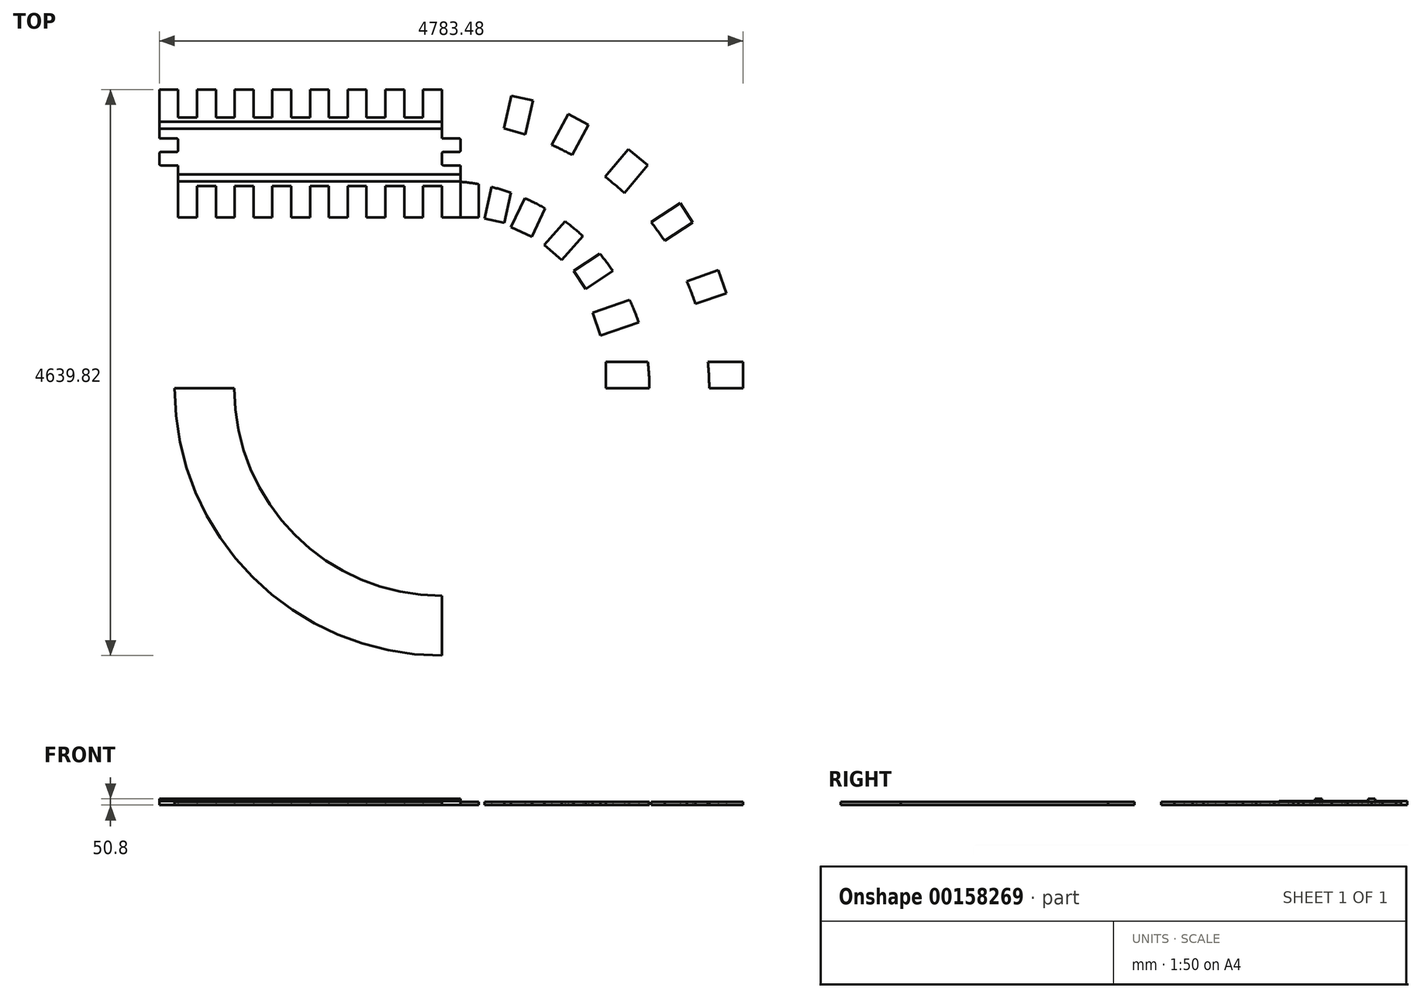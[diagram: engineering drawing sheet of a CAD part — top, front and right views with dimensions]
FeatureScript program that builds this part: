
annotation { "Feature Type Name" : "Feature", "Feature Type Description" : "" }
export const myFeature = defineFeature(function(context is Context, id is Id, definition is map)
    precondition{}
    {
        {
            var Q0;
            Q0=qCreatedBy(makeId("Top.planeOp"),FACE);
            var sketch = newSketch(context, id + "F0", { "sketchPlane" : qUnion([Q0])});
            skLineSegment(sketch, "E0", {"start": v(0, 0) * mm, "end": v(141.6, 0) * mm});
            skLineSegment(sketch, "E1", {"start": v(154.3, -12.7) * mm, "end": v(154.3, -97.3) * mm});
            skLineSegment(sketch, "E2", {"start": v(141.6, -110) * mm, "end": v(12.7, -110) * mm});
            skLineSegment(sketch, "E3", {"start": v(0, -122.7) * mm, "end": v(0, -207.32) * mm});
            skLineSegment(sketch, "E4", {"start": v(12.7, -220.02) * mm, "end": v(154.3, -220.02) * mm});
            skLineSegment(sketch, "E5", {"start": v(154.3, -220.02) * mm, "end": v(154.3, -647.87) * mm});
            skLineSegment(sketch, "E6", {"start": v(154.3, -647.87) * mm, "end": v(0, -647.87) * mm});
            skLineSegment(sketch, "E7", {"start": v(0, -647.87) * mm, "end": v(0, -389.82) * mm});
            skLineSegment(sketch, "E8", {"start": v(0, -389.82) * mm, "end": v(-154.3, -389.82) * mm});
            skLineSegment(sketch, "E9", {"start": v(-154.3, -389.82) * mm, "end": v(-154.3, -647.87) * mm});
            skLineSegment(sketch, "E10", {"start": v(-154.3, -647.87) * mm, "end": v(-308.61, -647.87) * mm});
            skLineSegment(sketch, "E11", {"start": v(-308.61, -647.87) * mm, "end": v(-308.61, -389.82) * mm});
            skLineSegment(sketch, "E12", {"start": v(-308.61, -389.82) * mm, "end": v(-462.92, -389.82) * mm});
            skLineSegment(sketch, "E13", {"start": v(-462.92, -389.82) * mm, "end": v(-462.92, -647.87) * mm});
            skLineSegment(sketch, "E14", {"start": v(-462.92, -647.87) * mm, "end": v(-617.22, -647.87) * mm});
            skLineSegment(sketch, "E15", {"start": v(-617.22, -647.87) * mm, "end": v(-617.22, -389.82) * mm});
            skLineSegment(sketch, "E16", {"start": v(-617.22, -389.82) * mm, "end": v(-771.53, -389.82) * mm});
            skLineSegment(sketch, "E17", {"start": v(-771.53, -389.82) * mm, "end": v(-771.53, -647.87) * mm});
            skLineSegment(sketch, "E18", {"start": v(-771.53, -647.87) * mm, "end": v(-925.83, -647.87) * mm});
            skLineSegment(sketch, "E19", {"start": v(-925.83, -647.87) * mm, "end": v(-925.83, -389.82) * mm});
            skPoint(sketch, "E20.visualSharp", {"position": v(154.3, 0) * mm});
            skArc(sketch, "E20.filletArc", {"start": v(154.3, -12.7) * mm, "mid": v(150.59, -3.72) * mm, "end": v(141.6, 0) * mm});
            skPoint(sketch, "E21.visualSharp", {"position": v(154.3, -110) * mm});
            skArc(sketch, "E21.filletArc", {"start": v(141.6, -110) * mm, "mid": v(150.59, -106.29) * mm, "end": v(154.3, -97.3) * mm});
            skPoint(sketch, "E22.visualSharp", {"position": v(0, -220.02) * mm});
            skArc(sketch, "E22.filletArc", {"start": v(0, -207.32) * mm, "mid": v(3.72, -216.3) * mm, "end": v(12.7, -220.02) * mm});
            skPoint(sketch, "E23.visualSharp", {"position": v(0, -110) * mm});
            skArc(sketch, "E23.filletArc", {"start": v(12.7, -110) * mm, "mid": v(3.72, -113.73) * mm, "end": v(0, -122.7) * mm});
            skLineSegment(sketch, "E24", {"start": v(-925.83, -389.82) * mm, "end": v(-1080.14, -389.82) * mm});
            skLineSegment(sketch, "E25", {"start": v(-1080.14, -389.82) * mm, "end": v(-1080.14, -647.87) * mm});
            skLineSegment(sketch, "E26", {"start": v(-1080.14, -647.87) * mm, "end": v(-1234.44, -647.87) * mm});
            skLineSegment(sketch, "E27", {"start": v(-1234.44, -647.87) * mm, "end": v(-1234.44, -389.82) * mm});
            skLineSegment(sketch, "E28", {"start": v(-1234.44, -389.82) * mm, "end": v(-1388.75, -389.82) * mm});
            skLineSegment(sketch, "E29", {"start": v(-1388.75, -389.82) * mm, "end": v(-1388.75, -647.87) * mm});
            skLineSegment(sketch, "E30", {"start": v(-1388.75, -647.87) * mm, "end": v(-1543.05, -647.87) * mm});
            skLineSegment(sketch, "E31", {"start": v(-1543.05, -647.87) * mm, "end": v(-1543.05, -389.82) * mm});
            skLineSegment(sketch, "E32", {"start": v(-1543.05, -389.82) * mm, "end": v(-1697.36, -389.82) * mm});
            skLineSegment(sketch, "E33", {"start": v(-1697.36, -389.82) * mm, "end": v(-1697.36, -647.87) * mm});
            skLineSegment(sketch, "E34", {"start": v(-1697.36, -647.87) * mm, "end": v(-1851.67, -647.87) * mm});
            skLineSegment(sketch, "E35", {"start": v(-1851.67, -647.87) * mm, "end": v(-1851.67, -389.82) * mm});
            skLineSegment(sketch, "E36", {"start": v(-1851.67, -389.82) * mm, "end": v(-2005.97, -389.82) * mm});
            skLineSegment(sketch, "E37", {"start": v(-2005.97, -389.82) * mm, "end": v(-2005.97, -647.87) * mm});
            skLineSegment(sketch, "E38", {"start": v(-2005.97, -647.87) * mm, "end": v(-2160.29, -647.87) * mm});
            skLineSegment(sketch, "E39", {"start": v(-2160.29, -647.87) * mm, "end": v(-2160.29, -220.02) * mm});
            skLineSegment(sketch, "E40", {"start": v(-2160.29, -220.02) * mm, "end": v(-2301.9, -220.02) * mm});
            skLineSegment(sketch, "E41", {"start": v(-2314.6, -207.32) * mm, "end": v(-2314.6, -122.7) * mm});
            skLineSegment(sketch, "E42", {"start": v(-2301.9, -110) * mm, "end": v(-2172.99, -110) * mm});
            skLineSegment(sketch, "E43", {"start": v(-2160.29, -97.3) * mm, "end": v(-2160.29, -12.7) * mm});
            skLineSegment(sketch, "E44", {"start": v(-2172.99, 0) * mm, "end": v(-2314.6, 0) * mm});
            skLineSegment(sketch, "E45", {"start": v(-2314.6, 0) * mm, "end": v(-2314.6, 399.88) * mm});
            skPoint(sketch, "E46.visualSharp", {"position": v(-2314.6, -110) * mm});
            skArc(sketch, "E46.filletArc", {"start": v(-2301.9, -110) * mm, "mid": v(-2310.87, -113.73) * mm, "end": v(-2314.6, -122.7) * mm});
            skPoint(sketch, "E47.visualSharp", {"position": v(-2314.6, -220.02) * mm});
            skArc(sketch, "E47.filletArc", {"start": v(-2314.6, -207.32) * mm, "mid": v(-2310.87, -216.3) * mm, "end": v(-2301.9, -220.02) * mm});
            skPoint(sketch, "E48.visualSharp", {"position": v(-2160.29, -110) * mm});
            skArc(sketch, "E48.filletArc", {"start": v(-2172.99, -110) * mm, "mid": v(-2164, -106.29) * mm, "end": v(-2160.29, -97.3) * mm});
            skPoint(sketch, "E49.visualSharp", {"position": v(-2160.29, 0) * mm});
            skArc(sketch, "E49.filletArc", {"start": v(-2160.29, -12.7) * mm, "mid": v(-2164, -3.72) * mm, "end": v(-2172.99, 0) * mm});
            skLineSegment(sketch, "E50", {"start": v(-2314.6, 399.88) * mm, "end": v(-2160.29, 399.88) * mm});
            skLineSegment(sketch, "E51", {"start": v(-2160.29, 399.88) * mm, "end": v(-2160.29, 172.14) * mm});
            skLineSegment(sketch, "E52", {"start": v(-2160.29, 172.14) * mm, "end": v(-2005.98, 172.14) * mm});
            skLineSegment(sketch, "E53", {"start": v(-2005.98, 172.14) * mm, "end": v(-2005.98, 399.88) * mm});
            skLineSegment(sketch, "E54", {"start": v(-2005.98, 399.88) * mm, "end": v(-1851.68, 399.88) * mm});
            skLineSegment(sketch, "E55", {"start": v(-1851.68, 399.88) * mm, "end": v(-1851.68, 172.14) * mm});
            skLineSegment(sketch, "E56", {"start": v(-1851.68, 172.14) * mm, "end": v(-1697.37, 172.14) * mm});
            skLineSegment(sketch, "E57", {"start": v(-1697.37, 172.14) * mm, "end": v(-1697.37, 399.88) * mm});
            skLineSegment(sketch, "E58", {"start": v(-1697.37, 399.88) * mm, "end": v(-1543.07, 399.88) * mm});
            skLineSegment(sketch, "E59", {"start": v(-1543.07, 399.88) * mm, "end": v(-1543.07, 172.14) * mm});
            skLineSegment(sketch, "E60", {"start": v(-1543.07, 172.14) * mm, "end": v(-1388.76, 172.14) * mm});
            skLineSegment(sketch, "E61", {"start": v(-1388.76, 172.14) * mm, "end": v(-1388.76, 400.96) * mm});
            skLineSegment(sketch, "E62", {"start": v(-1388.76, 400.96) * mm, "end": v(-1234.46, 400.96) * mm});
            skLineSegment(sketch, "E63", {"start": v(-1234.46, 400.96) * mm, "end": v(-1234.46, 172.14) * mm});
            skLineSegment(sketch, "E64", {"start": v(-1234.46, 172.14) * mm, "end": v(-1080.15, 172.14) * mm});
            skLineSegment(sketch, "E65", {"start": v(-1080.15, 172.14) * mm, "end": v(-1080.15, 400.96) * mm});
            skLineSegment(sketch, "E66", {"start": v(-1080.15, 400.96) * mm, "end": v(-925.85, 400.96) * mm});
            skLineSegment(sketch, "E67", {"start": v(-925.85, 400.96) * mm, "end": v(-925.85, 172.14) * mm});
            skLineSegment(sketch, "E68", {"start": v(-925.85, 172.14) * mm, "end": v(-771.54, 172.14) * mm});
            skLineSegment(sketch, "E69", {"start": v(-771.54, 172.14) * mm, "end": v(-771.54, 400.96) * mm});
            skLineSegment(sketch, "E70", {"start": v(-771.54, 400.96) * mm, "end": v(-617.24, 400.96) * mm});
            skLineSegment(sketch, "E71", {"start": v(-617.24, 400.96) * mm, "end": v(-617.24, 172.14) * mm});
            skLineSegment(sketch, "E72", {"start": v(-617.24, 172.14) * mm, "end": v(-462.93, 172.14) * mm});
            skLineSegment(sketch, "E73", {"start": v(-462.93, 172.14) * mm, "end": v(-462.93, 400.96) * mm});
            skLineSegment(sketch, "E74", {"start": v(-462.93, 400.96) * mm, "end": v(-308.63, 400.96) * mm});
            skLineSegment(sketch, "E75", {"start": v(-308.63, 400.96) * mm, "end": v(-308.63, 172.14) * mm});
            skLineSegment(sketch, "E76", {"start": v(-308.63, 172.14) * mm, "end": v(-154.32, 172.14) * mm});
            skLineSegment(sketch, "E77", {"start": v(-154.32, 172.14) * mm, "end": v(-154.32, 400.96) * mm});
            skLineSegment(sketch, "E78", {"start": v(-154.32, 400.96) * mm, "end": v(-0.02, 400.96) * mm});
            skLineSegment(sketch, "E79", {"start": v(-0.02, 400.96) * mm, "end": v(-0.02, 172.14) * mm});
            skLineSegment(sketch, "E80", {"start": v(-0.02, 172.14) * mm, "end": v(0, 0) * mm});
            skSolve(sketch);
        }
        {
            var Q0;
            Q0=makeQuery(id+"F0.imprint","IMPRINT",FACE,{"disambiguationData":[TD([[makeQuery(id+"F0.imprint","IMPRINT",EDGE,{"derivedFrom":sQuery(id+"F0.wireOp",EDGE,"E0")}),-1.0]])]});
            var sketch = newSketch(context, id + "F1", { "sketchPlane" : qUnion([Q0])});
            skLineSegment(sketch, "E81", {"start": v(-2314.86, 138.26) * mm, "end": v(0, 138.26) * mm});
            skLineSegment(sketch, "E82.0", {"start": v(-2314.86, 81.11) * mm, "end": v(0, 81.11) * mm});
            skLineSegment(sketch, "E83", {"start": v(-2160.59, -353.29) * mm, "end": v(154.12, -353.29) * mm});
            skLineSegment(sketch, "E84.0", {"start": v(-2160.59, -296.14) * mm, "end": v(154.12, -296.14) * mm});
            skLineSegment(sketch, "E85", {"start": v(-2314.86, 138.26) * mm, "end": v(-2314.86, 81.11) * mm});
            skLineSegment(sketch, "E86", {"start": v(-2160.59, -296.14) * mm, "end": v(-2160.59, -353.29) * mm});
            skLineSegment(sketch, "E87", {"start": v(154.12, -296.14) * mm, "end": v(154.12, -353.29) * mm});
            skLineSegment(sketch, "E88", {"start": v(0, 138.26) * mm, "end": v(0, 81.11) * mm});
            skSolve(sketch);
        }
        {
            var Q0;
            Q0=qSketchRegion(id+"F0",true);
            extrude(context, id + "F2", {"entities" : qUnion([Q0]), "depth" : 31.75 * mm});
        }
        {
            var Q0;
            Q0=qSketchRegion(id+"F1",true);
            extrude(context, id + "F3", {"entities" : qUnion([Q0]), "operationType" : NewBodyOperationType.ADD, "depth" : 50.8 * mm});
        }
        {
            var Q0;
            Q0=qCreatedBy(makeId("Top.planeOp"),FACE);
            var sketch = newSketch(context, id + "F4", { "sketchPlane" : qUnion([Q0])});
            skCircle(sketch, "E89", {"center": v(0, -2048.58) * mm, "radius": 2190.28 * mm});
            skCircle(sketch, "E90", {"center": v(0, -2048.58) * mm, "radius": 1700.76 * mm});
            skLineSegment(sketch, "E91", {"start": v(0, -4987.67) * mm, "end": v(0, 1254.96) * mm});
            skLineSegment(sketch, "E92", {"start": v(-3366.62, -2048.58) * mm, "end": v(3747.67, -2048.58) * mm});
            skLineSegment(sketch, "E93", {"start": v(0, 141.7) * mm, "end": v(0, 0) * mm});
            skLineSegment(sketch, "E94", {"start": v(0, 0) * mm, "end": v(142.26, 0) * mm});
            skLineSegment(sketch, "E95", {"start": v(154.96, -12.7) * mm, "end": v(154.96, -96.46) * mm});
            skLineSegment(sketch, "E96", {"start": v(142.26, -109.16) * mm, "end": v(12.7, -109.16) * mm});
            skLineSegment(sketch, "E97", {"start": v(0, -121.86) * mm, "end": v(0, -207.92) * mm});
            skLineSegment(sketch, "E98", {"start": v(12.7, -220.62) * mm, "end": v(153.58, -220.62) * mm});
            skLineSegment(sketch, "E99", {"start": v(153.58, -220.62) * mm, "end": v(153.58, -354.76) * mm});
            skPoint(sketch, "E100.visualSharp", {"position": v(154.96, 0) * mm});
            skArc(sketch, "E100.filletArc", {"start": v(154.96, -12.7) * mm, "mid": v(151.24, -3.72) * mm, "end": v(142.26, 0) * mm});
            skPoint(sketch, "E101.visualSharp", {"position": v(154.96, -109.16) * mm});
            skArc(sketch, "E101.filletArc", {"start": v(142.26, -109.16) * mm, "mid": v(151.24, -105.44) * mm, "end": v(154.96, -96.46) * mm});
            skPoint(sketch, "E102.visualSharp", {"position": v(0, -220.62) * mm});
            skArc(sketch, "E102.filletArc", {"start": v(0, -207.92) * mm, "mid": v(3.72, -216.9) * mm, "end": v(12.7, -220.62) * mm});
            skPoint(sketch, "E103.visualSharp", {"position": v(0, -109.16) * mm});
            skArc(sketch, "E103.filletArc", {"start": v(12.7, -109.16) * mm, "mid": v(3.72, -112.88) * mm, "end": v(0, -121.86) * mm});
            skLineSegment(sketch, "E104", {"start": v(0, 141.7) * mm, "end": v(0, 400.95) * mm});
            skLineSegment(sketch, "E105", {"start": v(0, 400.95) * mm, "end": v(152.02, 400.95) * mm});
            skLineSegment(sketch, "E106", {"start": v(152.02, 400.95) * mm, "end": v(152.02, 136.42) * mm});
            skLineSegment(sketch, "E107", {"start": v(900.1, -51.79) * mm, "end": v(1034.84, 199.45) * mm});
            skLineSegment(sketch, "E108", {"start": v(1034.84, 199.45) * mm, "end": v(1199.5, 111.15) * mm});
            skLineSegment(sketch, "E109", {"start": v(1199.5, 111.15) * mm, "end": v(1067.06, -135.8) * mm});
            skLineSegment(sketch, "E110", {"start": v(1714.15, -685.11) * mm, "end": v(1954.38, -530.86) * mm});
            skLineSegment(sketch, "E111", {"start": v(1954.38, -530.86) * mm, "end": v(2056.05, -689.2) * mm});
            skLineSegment(sketch, "E112", {"start": v(2056.05, -689.2) * mm, "end": v(1825.03, -837.55) * mm});
            skLineSegment(sketch, "E113", {"start": v(508.33, 81.9) * mm, "end": v(568.73, 351) * mm});
            skLineSegment(sketch, "E114", {"start": v(568.73, 351) * mm, "end": v(747.33, 310.92) * mm});
            skLineSegment(sketch, "E115", {"start": v(747.33, 310.92) * mm, "end": v(684.71, 31.93) * mm});
            skLineSegment(sketch, "E116", {"start": v(1338.6, -314.95) * mm, "end": v(1527.03, -87.62) * mm});
            skLineSegment(sketch, "E117", {"start": v(1527.03, -87.62) * mm, "end": v(1684.9, -218.47) * mm});
            skLineSegment(sketch, "E118", {"start": v(1684.9, -218.47) * mm, "end": v(1494.87, -447.74) * mm});
            skLineSegment(sketch, "E119", {"start": v(2006.14, -1169.52) * mm, "end": v(2265.44, -1079.33) * mm});
            skLineSegment(sketch, "E120", {"start": v(2265.44, -1079.33) * mm, "end": v(2331.04, -1267.93) * mm});
            skLineSegment(sketch, "E121", {"start": v(2331.04, -1267.93) * mm, "end": v(2077.9, -1355.98) * mm});
            skLineSegment(sketch, "E122", {"start": v(2179.55, -1832.02) * mm, "end": v(2468.62, -1832.02) * mm});
            skLineSegment(sketch, "E123", {"start": v(2468.62, -1832.02) * mm, "end": v(2468.62, -2048.58) * mm});
            skLineSegment(sketch, "E124", {"start": v(153.58, -354.76) * mm, "end": v(153.58, -647.34) * mm});
            skLineSegment(sketch, "E125", {"start": v(153.58, -647.34) * mm, "end": v(303.64, -647.34) * mm});
            skLineSegment(sketch, "E126", {"start": v(303.64, -647.34) * mm, "end": v(303.64, -375.14) * mm});
            skLineSegment(sketch, "E127", {"start": v(406.51, -397.11) * mm, "end": v(350.84, -655.51) * mm});
            skLineSegment(sketch, "E128", {"start": v(350.84, -655.51) * mm, "end": v(511.42, -690.1) * mm});
            skLineSegment(sketch, "E129", {"start": v(511.42, -690.1) * mm, "end": v(564.4, -444.2) * mm});
            skLineSegment(sketch, "E130", {"start": v(678.89, -489.18) * mm, "end": v(566.54, -725.25) * mm});
            skLineSegment(sketch, "E131", {"start": v(566.54, -725.25) * mm, "end": v(735.75, -805.78) * mm});
            skLineSegment(sketch, "E132", {"start": v(735.75, -805.78) * mm, "end": v(846.35, -573.36) * mm});
            skLineSegment(sketch, "E133", {"start": v(1009.64, -679.92) * mm, "end": v(840.33, -871.76) * mm});
            skLineSegment(sketch, "E134", {"start": v(840.33, -871.76) * mm, "end": v(981.8, -996.63) * mm});
            skLineSegment(sketch, "E135", {"start": v(981.8, -996.63) * mm, "end": v(1155.12, -800.27) * mm});
            skLineSegment(sketch, "E136", {"start": v(1293.87, -944.72) * mm, "end": v(1081.5, -1084.9) * mm});
            skLineSegment(sketch, "E137", {"start": v(1081.5, -1084.9) * mm, "end": v(1179.42, -1233.25) * mm});
            skLineSegment(sketch, "E138", {"start": v(1179.42, -1233.25) * mm, "end": v(1402.27, -1086.17) * mm});
            skLineSegment(sketch, "E139", {"start": v(1538.53, -1323.66) * mm, "end": v(1235.92, -1427.35) * mm});
            skLineSegment(sketch, "E140", {"start": v(1235.92, -1427.35) * mm, "end": v(1299.82, -1613.82) * mm});
            skLineSegment(sketch, "E141", {"start": v(1299.82, -1613.82) * mm, "end": v(1612.16, -1506.8) * mm});
            skLineSegment(sketch, "E142", {"start": v(1686.92, -1832.02) * mm, "end": v(1342.87, -1832.02) * mm});
            skLineSegment(sketch, "E143", {"start": v(1342.87, -1832.02) * mm, "end": v(1342.87, -2048.58) * mm});
            skSolve(sketch);
        }
        {
            var Q0;
            {var subQ0=sQuery(id+"F4.wireOp",EDGE,"E91");var subQ1=sQuery(id+"F4.wireOp",EDGE,"E89");var subQ2=makeQuery(id+"F4.imprint","INTERSECT",VERTEX,{"disambiguationData":[OD(0.0)],"derivedFrom":[subQ1,subQ0]});Q0=makeQuery(id+"F4.imprint","IMPRINT",FACE,{"disambiguationData":[TD([[makeQuery(id+"F4.imprint","IMPRINT",EDGE,{"disambiguationData":[TD([[subQ2,1.0]])],"derivedFrom":subQ1}),1.0]])]});}
            var Q1;
            {var subQ1=sQuery(id+"F4.wireOp",EDGE,"E93");Q1=makeQuery(id+"F4.imprint","IMPRINT",FACE,{"disambiguationData":[TD([[makeQuery(id+"F4.imprint","IMPRINT",EDGE,{"derivedFrom":subQ1}),1.0]])]});}
            var Q2;
            {var subQ0=sQuery(id+"F4.wireOp",EDGE,"E113");Q2=makeQuery(id+"F4.imprint","IMPRINT",FACE,{"disambiguationData":[TD([[makeQuery(id+"F4.imprint","IMPRINT",EDGE,{"derivedFrom":subQ0}),-1.0]])]});}
            var Q3;
            {var subQ0=sQuery(id+"F4.wireOp",EDGE,"E104");Q3=makeQuery(id+"F4.imprint","IMPRINT",FACE,{"disambiguationData":[TD([[makeQuery(id+"F4.imprint","IMPRINT",EDGE,{"derivedFrom":subQ0}),-1.0]])]});}
            var Q4;
            {var subQ0=sQuery(id+"F4.wireOp",EDGE,"E107");Q4=makeQuery(id+"F4.imprint","IMPRINT",FACE,{"disambiguationData":[TD([[makeQuery(id+"F4.imprint","IMPRINT",EDGE,{"derivedFrom":subQ0}),-1.0]])]});}
            var Q5;
            {var subQ0=sQuery(id+"F4.wireOp",EDGE,"E124");Q5=makeQuery(id+"F4.imprint","IMPRINT",FACE,{"disambiguationData":[TD([[makeQuery(id+"F4.imprint","IMPRINT",EDGE,{"derivedFrom":subQ0}),1.0]])]});}
            var Q6;
            {var subQ0=sQuery(id+"F4.wireOp",EDGE,"E127");Q6=makeQuery(id+"F4.imprint","IMPRINT",FACE,{"disambiguationData":[TD([[makeQuery(id+"F4.imprint","IMPRINT",EDGE,{"derivedFrom":subQ0}),1.0]])]});}
            var Q7;
            {var subQ0=sQuery(id+"F4.wireOp",EDGE,"E130");Q7=makeQuery(id+"F4.imprint","IMPRINT",FACE,{"disambiguationData":[TD([[makeQuery(id+"F4.imprint","IMPRINT",EDGE,{"derivedFrom":subQ0}),1.0]])]});}
            var Q8;
            {var subQ0=sQuery(id+"F4.wireOp",EDGE,"E133");Q8=makeQuery(id+"F4.imprint","IMPRINT",FACE,{"disambiguationData":[TD([[makeQuery(id+"F4.imprint","IMPRINT",EDGE,{"derivedFrom":subQ0}),1.0]])]});}
            var Q9;
            {var subQ0=sQuery(id+"F4.wireOp",EDGE,"E136");Q9=makeQuery(id+"F4.imprint","IMPRINT",FACE,{"disambiguationData":[TD([[makeQuery(id+"F4.imprint","IMPRINT",EDGE,{"derivedFrom":subQ0}),1.0]])]});}
            var Q10;
            {var subQ0=sQuery(id+"F4.wireOp",EDGE,"E139");Q10=makeQuery(id+"F4.imprint","IMPRINT",FACE,{"disambiguationData":[TD([[makeQuery(id+"F4.imprint","IMPRINT",EDGE,{"derivedFrom":subQ0}),1.0]])]});}
            var Q11;
            {var subQ0=sQuery(id+"F4.wireOp",EDGE,"E142");Q11=makeQuery(id+"F4.imprint","IMPRINT",FACE,{"disambiguationData":[TD([[makeQuery(id+"F4.imprint","IMPRINT",EDGE,{"derivedFrom":subQ0}),1.0]])]});}
            var Q12;
            {var subQ0=sQuery(id+"F4.wireOp",EDGE,"E122");Q12=makeQuery(id+"F4.imprint","IMPRINT",FACE,{"disambiguationData":[TD([[makeQuery(id+"F4.imprint","IMPRINT",EDGE,{"derivedFrom":subQ0}),-1.0]])]});}
            var Q13;
            {var subQ0=sQuery(id+"F4.wireOp",EDGE,"E119");Q13=makeQuery(id+"F4.imprint","IMPRINT",FACE,{"disambiguationData":[TD([[makeQuery(id+"F4.imprint","IMPRINT",EDGE,{"derivedFrom":subQ0}),-1.0]])]});}
            var Q14;
            {var subQ0=sQuery(id+"F4.wireOp",EDGE,"E110");Q14=makeQuery(id+"F4.imprint","IMPRINT",FACE,{"disambiguationData":[TD([[makeQuery(id+"F4.imprint","IMPRINT",EDGE,{"derivedFrom":subQ0}),-1.0]])]});}
            var Q15;
            {var subQ0=sQuery(id+"F4.wireOp",EDGE,"E116");Q15=makeQuery(id+"F4.imprint","IMPRINT",FACE,{"disambiguationData":[TD([[makeQuery(id+"F4.imprint","IMPRINT",EDGE,{"derivedFrom":subQ0}),-1.0]])]});}
            extrude(context, id + "F5", {"entities" : qUnion([Q0, Q1, Q2, Q3, Q4, Q5, Q6, Q7, Q8, Q9, Q10, Q11, Q12, Q13, Q14, Q15]), "operationType" : NewBodyOperationType.ADD, "depth" : 25.4 * mm});
        }
    });
